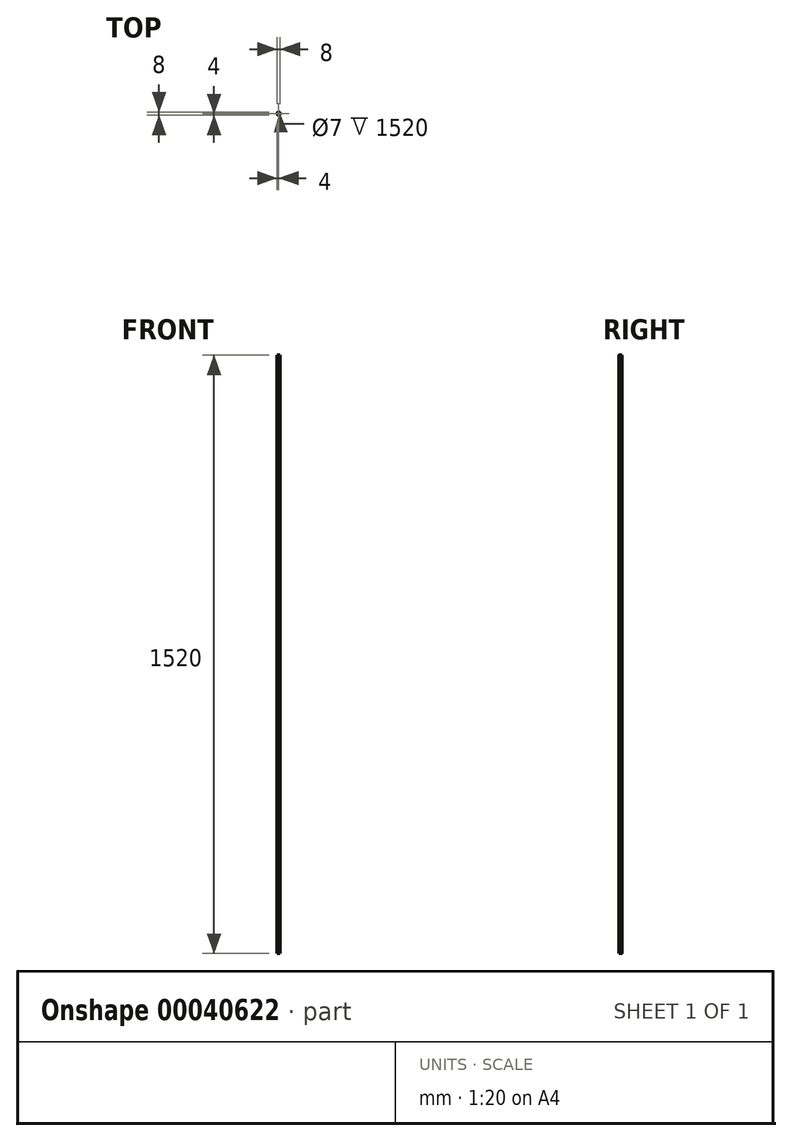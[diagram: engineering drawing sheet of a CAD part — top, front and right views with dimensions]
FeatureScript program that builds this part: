
annotation { "Feature Type Name" : "Feature", "Feature Type Description" : "" }
export const myFeature = defineFeature(function(context is Context, id is Id, definition is map)
    precondition{}
    {
        {
            var Q0;
            Q0=qCreatedBy(makeId("Top.planeOp"),FACE);
            var sketch = newSketch(context, id + "F0", { "sketchPlane" : qUnion([Q0])});
            skCircle(sketch, "E0", {"center": v(0, 0) * mm, "radius": 4 * mm});
            skCircle(sketch, "E1", {"center": v(0, 0) * mm, "radius": 3.5 * mm});
            skSolve(sketch);
        }
        {
            var Q0;
            Q0=makeQuery(id+"F0.imprint","IMPRINT",FACE,{"disambiguationData":[TD([[makeQuery(id+"F0.imprint","IMPRINT",EDGE,{"derivedFrom":sQuery(id+"F0.wireOp",EDGE,"E0")}),1.0]])]});
            extrude(context, id + "F1", {"entities" : qUnion([Q0]), "depth" : 1520 * mm});
        }
    });
